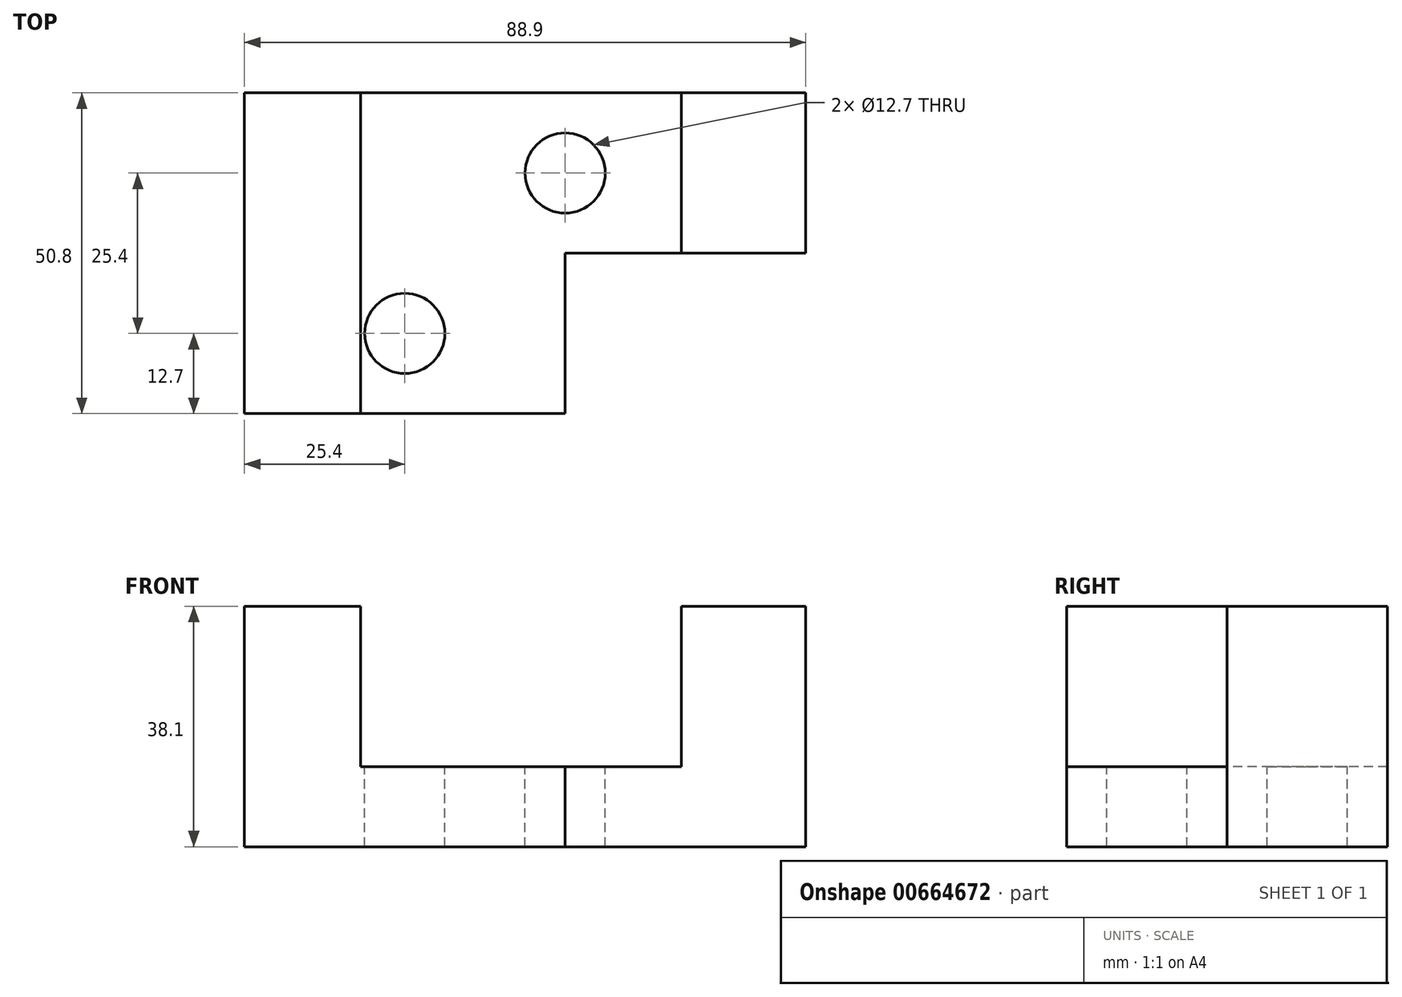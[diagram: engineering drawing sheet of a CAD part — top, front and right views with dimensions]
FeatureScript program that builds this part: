
annotation { "Feature Type Name" : "Feature", "Feature Type Description" : "" }
export const myFeature = defineFeature(function(context is Context, id is Id, definition is map)
    precondition{}
    {
        {
            var Q0;
            Q0=qCreatedBy(makeId("Front.planeOp"),FACE);
            var sketch = newSketch(context, id + "F0", { "sketchPlane" : qUnion([Q0])});
            skLineSegment(sketch, "E0.bottom", {"start": v(-44.45, 19.05) * mm, "end": v(44.45, 19.05) * mm});
            skLineSegment(sketch, "E0.top", {"start": v(-44.45, -19.05) * mm, "end": v(44.45, -19.05) * mm});
            skLineSegment(sketch, "E0.left", {"start": v(-44.45, 19.05) * mm, "end": v(-44.45, -19.05) * mm});
            skLineSegment(sketch, "E0.right", {"start": v(44.45, 19.05) * mm, "end": v(44.45, -19.05) * mm});
            skPoint(sketch, "E0.middle", {"position": v(0, 0) * mm});
            skSolve(sketch);
        }
        {
            var Q0;
            Q0=makeQuery(id+"F0.imprint","IMPRINT",FACE,{"disambiguationData":[TD([[makeQuery(id+"F0.imprint","IMPRINT",EDGE,{"derivedFrom":sQuery(id+"F0.wireOp",EDGE,"E0.bottom")}),-1.0]])]});
            extrude(context, id + "F1", {"entities" : qUnion([Q0]), "depth" : 50.8 * mm, "offsetDistance" : 25.4 * mm});
        }
        {
            var Q0;
            Q0=makeQuery(id+"F1.opExtrude","CAP_FACE",FACE,{"disambiguationData":[OSD([sQuery(id+"F0.wireOp",EDGE,"E0.bottom"),sQuery(id+"F0.wireOp",EDGE,"E0.top"),sQuery(id+"F0.wireOp",EDGE,"E0.left"),sQuery(id+"F0.wireOp",EDGE,"E0.right")])],"isStart":false});
            var sketch = newSketch(context, id + "F2", { "sketchPlane" : qUnion([Q0])});
            skLineSegment(sketch, "E1.bottom", {"start": v(-26.06, 19.05) * mm, "end": v(24.74, 19.05) * mm});
            skLineSegment(sketch, "E1.top", {"start": v(-26.06, -6.35) * mm, "end": v(24.74, -6.35) * mm});
            skLineSegment(sketch, "E1.left", {"start": v(-26.06, 19.05) * mm, "end": v(-26.06, -6.35) * mm});
            skLineSegment(sketch, "E1.right", {"start": v(24.74, 19.05) * mm, "end": v(24.74, -6.35) * mm});
            skSolve(sketch);
        }
        {
            var Q0;
            Q0=makeQuery(id+"F2.imprint","IMPRINT",FACE,{"disambiguationData":[TD([[makeQuery(id+"F2.imprint","IMPRINT",EDGE,{"derivedFrom":sQuery(id+"F2.wireOp",EDGE,"E1.bottom")}),-1.0]])]});
            extrude(context, id + "F3", {"entities" : qUnion([Q0]), "operationType" : NewBodyOperationType.REMOVE, "endBound" : BoundingType.THROUGH_ALL, "oppositeDirection" : true, "depth" : 25.4 * mm, "offsetDistance" : 25.4 * mm});
        }
        {
            var Q0;
            {var subQ0=sQuery(id+"F0.wireOp",EDGE,"E0.right");var subQ3=sQuery(id+"F0.wireOp",EDGE,"E0.bottom");Q0=makeQuery(id+"F3.boolean.opBoolean","SPLIT",FACE,{"disambiguationData":[TD([makeQuery(id+"F1.opExtrude","SWEPT_FACE",FACE,{"disambiguationData":[OSD([subQ0])]})])],"derivedFrom":makeQuery(id+"F1.opExtrude","SWEPT_FACE",FACE,{"disambiguationData":[OSD([subQ3])]})});}
            var sketch = newSketch(context, id + "F4", { "sketchPlane" : qUnion([Q0])});
            skLineSegment(sketch, "E2.bottom", {"start": v(44.45, -50.8) * mm, "end": v(6.35, -50.8) * mm});
            skLineSegment(sketch, "E2.top", {"start": v(44.45, -25.4) * mm, "end": v(6.35, -25.4) * mm});
            skLineSegment(sketch, "E2.left", {"start": v(44.45, -50.8) * mm, "end": v(44.45, -25.4) * mm});
            skLineSegment(sketch, "E2.right", {"start": v(6.35, -50.8) * mm, "end": v(6.35, -25.4) * mm});
            skSolve(sketch);
        }
        {
            var Q0;
            Q0 = qSketchRegion(id + "F4", true);
            extrude(context, id + "F5", {"entities" : qUnion([Q0]), "operationType" : NewBodyOperationType.REMOVE, "endBound" : BoundingType.THROUGH_ALL, "oppositeDirection" : true, "depth" : 25.4 * mm, "offsetDistance" : 25.4 * mm});
        }
        {
            var Q0;
            Q0=makeQuery(id+"F3.boolean.opBoolean","COPY",FACE,{"derivedFrom":makeQuery(id+"F3.opExtrude","SWEPT_FACE",FACE,{"disambiguationData":[OSD([sQuery(id+"F2.wireOp",EDGE,"E1.top")])]})});
            var sketch = newSketch(context, id + "F6", { "sketchPlane" : qUnion([Q0])});
            skCircle(sketch, "E3", {"center": v(6.35, -12.7) * mm, "radius": 6.35 * mm});
            skCircle(sketch, "E4", {"center": v(-19.05, -38.1) * mm, "radius": 6.35 * mm});
            skSolve(sketch);
        }
        {
            var Q0;
            Q0 = qSketchRegion(id + "F6", true);
            extrude(context, id + "F7", {"entities" : qUnion([Q0]), "operationType" : NewBodyOperationType.REMOVE, "endBound" : BoundingType.THROUGH_ALL, "oppositeDirection" : true, "depth" : 25.4 * mm, "offsetDistance" : 25.4 * mm});
        }
    });
